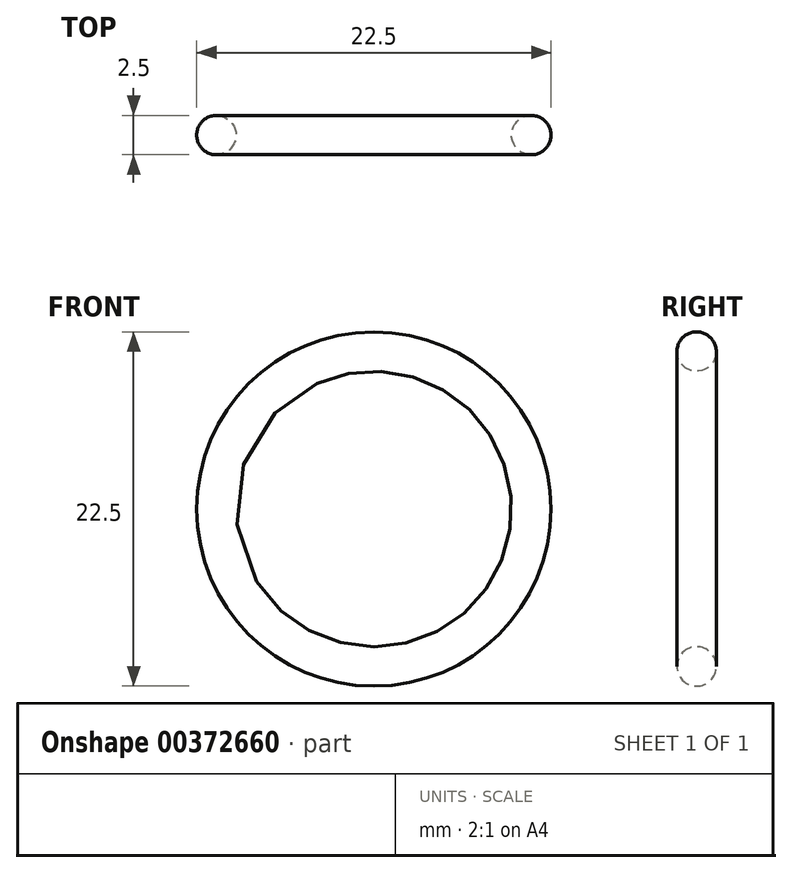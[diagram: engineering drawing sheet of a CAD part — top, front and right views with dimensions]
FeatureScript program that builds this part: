
annotation { "Feature Type Name" : "Feature", "Feature Type Description" : "" }
export const myFeature = defineFeature(function(context is Context, id is Id, definition is map)
    precondition{}
    {
        {
            var Q0;
            Q0=qCreatedBy(makeId("Top.planeOp"),FACE);
            var sketch = newSketch(context, id + "F0", { "sketchPlane" : qUnion([Q0])});
            skCircle(sketch, "E0", {"center": v(10, 0) * mm, "radius": 1.25 * mm});
            skLineSegment(sketch, "E1", {"start": v(0, 0) * mm, "end": v(0, 6.55) * mm, "construction": true});
            skSolve(sketch);
        }
        {
            var Q0;
            Q0=makeQuery(id+"F0.imprint","IMPRINT",FACE,{"disambiguationData":[TD([[makeQuery(id+"F0.imprint","IMPRINT",EDGE,{"derivedFrom":sQuery(id+"F0.wireOp",EDGE,"E0")}),1.0]])]});
            var Q1;
            Q1=sQuery(id+"F0.wireOp",EDGE,"E1");
            revolve(context, id + "F1", {"surfaceOperationType" : NewSurfaceOperationType.NEW, "entities" : qUnion([Q0]), "axis" : qUnion([Q1]), "revolveType" : RevolveType.FULL});
        }
    });
